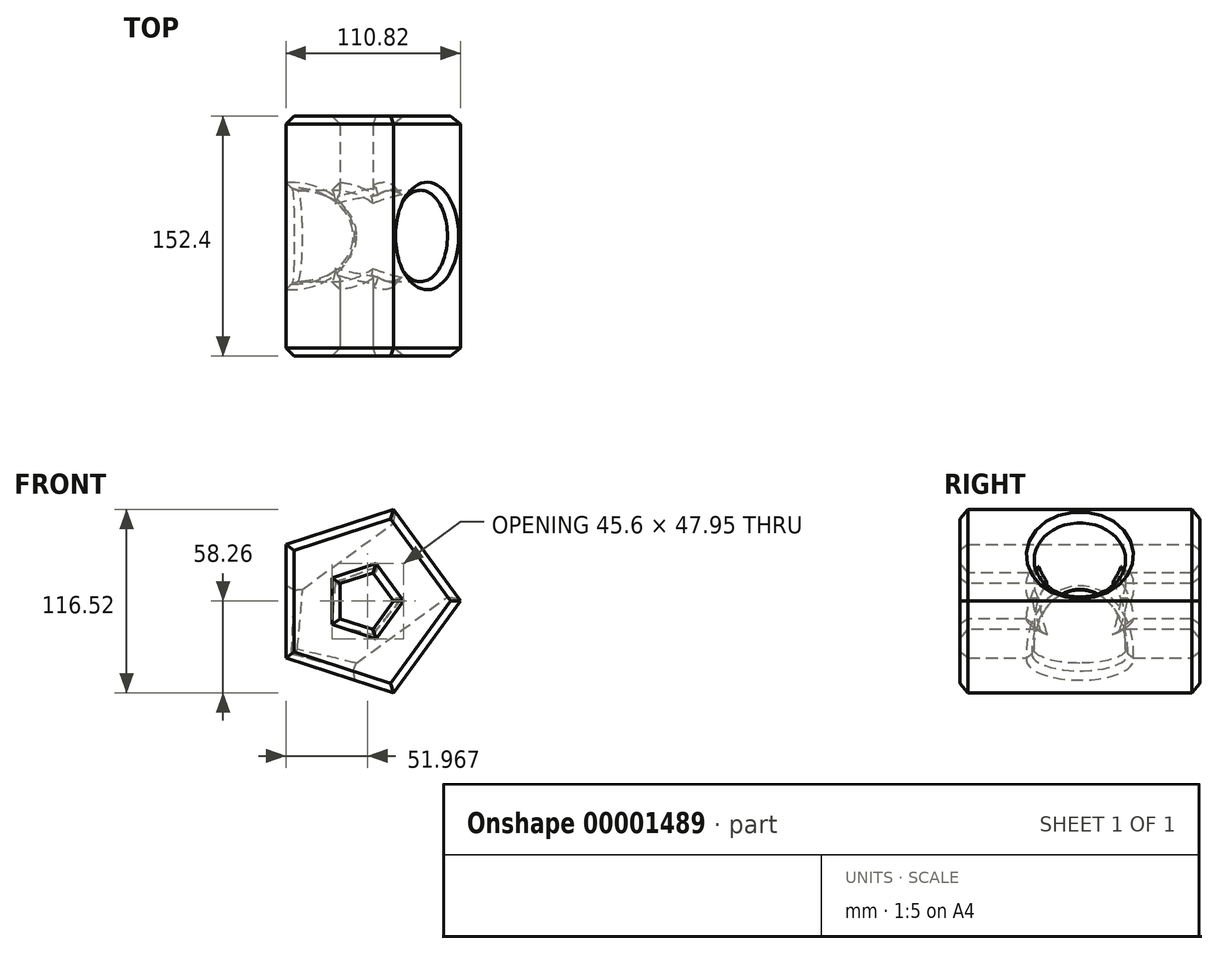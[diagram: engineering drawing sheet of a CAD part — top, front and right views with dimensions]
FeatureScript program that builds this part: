
annotation { "Feature Type Name" : "Feature", "Feature Type Description" : "" }
export const myFeature = defineFeature(function(context is Context, id is Id, definition is map)
    precondition{}
    {
        {
            var Q0;
            Q0=qCreatedBy(makeId("Front.planeOp"),FACE);
            var sketch = newSketch(context, id + "F0", { "sketchPlane" : qUnion([Q0])});
            skCircle(sketch, "E0.cCircle", {"center": v(0, 0) * mm, "radius": 49.56 * mm, "construction": true});
            skLineSegment(sketch, "E0.0", {"start": v(-49.56, -36) * mm, "end": v(-49.56, 36) * mm});
            skLineSegment(sketch, "E0.1", {"start": v(-49.56, 36) * mm, "end": v(18.93, 58.26) * mm});
            skLineSegment(sketch, "E0.2", {"start": v(18.93, 58.26) * mm, "end": v(61.26, 0) * mm});
            skLineSegment(sketch, "E0.3", {"start": v(61.26, 0) * mm, "end": v(18.93, -58.26) * mm});
            skLineSegment(sketch, "E0.4", {"start": v(18.93, -58.26) * mm, "end": v(-49.56, -36) * mm});
            skPoint(sketch, "E0.0.midPoint", {"position": v(-49.56, 0) * mm});
            skLineSegment(sketch, "E1", {"start": v(-49.56, 36) * mm, "end": v(41.4, -27.24) * mm});
            skSolve(sketch);
        }
        {
            var Q0;
            Q0=makeQuery(id+"F0.imprint","IMPRINT",FACE,{"disambiguationData":[TD([[makeQuery(id+"F0.imprint","IMPRINT",EDGE,{"derivedFrom":sQuery(id+"F0.wireOp",EDGE,"E0.0")}),-1.0]])]});
            extrude(context, id + "F1", {"entities" : qUnion([Q0]), "depth" : 152.4 * mm});
        }
        {
            var Q0;
            Q0=makeQuery(id+"F1.opExtrude","SWEPT_FACE",FACE,{"disambiguationData":[OSD([sQuery(id+"F0.wireOp",EDGE,"E0.2")])]});
            var sketch = newSketch(context, id + "F2", { "sketchPlane" : qUnion([Q0])});
            skLineSegment(sketch, "E2", {"start": v(0, 0) * mm, "end": v(-152.4, 0) * mm, "construction": true});
            skLineSegment(sketch, "E3", {"start": v(-76.2, 36) * mm, "end": v(-76.2, -36) * mm, "construction": true});
            skCircle(sketch, "E4", {"center": v(-76.2, 0) * mm, "radius": 29.02 * mm});
            skSolve(sketch);
        }
        {
            var Q0;
            Q0=makeQuery(id+"F2.imprint","IMPRINT",FACE,{"disambiguationData":[TD([[makeQuery(id+"F2.imprint","IMPRINT",EDGE,{"derivedFrom":sQuery(id+"F2.wireOp",EDGE,"E4")}),1.0]])]});
            extrude(context, id + "F3", {"entities" : qUnion([Q0]), "operationType" : NewBodyOperationType.REMOVE, "endBound" : BoundingType.THROUGH_ALL, "oppositeDirection" : true, "depth" : 25.4 * mm});
        }
        {
            var Q0;
            Q0=makeQuery(id+"F1.opExtrude","CAP_FACE",FACE,{"disambiguationData":[OSD([sQuery(id+"F0.wireOp",EDGE,"E0.0"),sQuery(id+"F0.wireOp",EDGE,"E0.1"),sQuery(id+"F0.wireOp",EDGE,"E0.2"),sQuery(id+"F0.wireOp",EDGE,"E0.3"),sQuery(id+"F0.wireOp",EDGE,"E0.4")])],"isStart":false});
            var sketch = newSketch(context, id + "F4", { "sketchPlane" : qUnion([Q0])});
            skLineSegment(sketch, "E5", {"start": v(61.26, 0) * mm, "end": v(-49.56, 0) * mm, "construction": true});
            skLineSegment(sketch, "E6", {"start": v(18.93, 58.26) * mm, "end": v(18.93, -58.26) * mm, "construction": true});
            skCircle(sketch, "E7.cCircle", {"center": v(0, 0) * mm, "radius": 15.31 * mm, "construction": true});
            skLineSegment(sketch, "E7.0", {"start": v(18.93, 0) * mm, "end": v(5.85, -18) * mm});
            skLineSegment(sketch, "E7.1", {"start": v(5.85, -18) * mm, "end": v(-15.31, -11.13) * mm});
            skLineSegment(sketch, "E7.2", {"start": v(-15.31, -11.13) * mm, "end": v(-15.31, 11.13) * mm});
            skLineSegment(sketch, "E7.3", {"start": v(-15.31, 11.13) * mm, "end": v(5.85, 18) * mm});
            skLineSegment(sketch, "E7.4", {"start": v(5.85, 18) * mm, "end": v(18.93, 0) * mm});
            skPoint(sketch, "E7.0.midPoint", {"position": v(12.39, -9) * mm});
            skSolve(sketch);
        }
        {
            var Q0;
            Q0=makeQuery(id+"F4.imprint","IMPRINT",FACE,{"disambiguationData":[TD([[makeQuery(id+"F4.imprint","IMPRINT",EDGE,{"derivedFrom":sQuery(id+"F4.wireOp",EDGE,"E7.0")}),-1.0]])]});
            extrude(context, id + "F5", {"entities" : qUnion([Q0]), "operationType" : NewBodyOperationType.REMOVE, "endBound" : BoundingType.THROUGH_ALL, "oppositeDirection" : true, "depth" : 25.4 * mm});
        }
        {
            var Q0;
            Q0=makeQuery(id+"F1.opExtrude","CAP_FACE",FACE,{"disambiguationData":[OSD([sQuery(id+"F0.wireOp",EDGE,"E0.0"),sQuery(id+"F0.wireOp",EDGE,"E0.1"),sQuery(id+"F0.wireOp",EDGE,"E0.2"),sQuery(id+"F0.wireOp",EDGE,"E0.3"),sQuery(id+"F0.wireOp",EDGE,"E0.4")])],"isStart":false});
            var Q1;
            Q1=makeQuery(id+"F1.opExtrude","CAP_FACE",FACE,{"disambiguationData":[OSD([sQuery(id+"F0.wireOp",EDGE,"E0.0"),sQuery(id+"F0.wireOp",EDGE,"E0.1"),sQuery(id+"F0.wireOp",EDGE,"E0.2"),sQuery(id+"F0.wireOp",EDGE,"E0.3"),sQuery(id+"F0.wireOp",EDGE,"E0.4")])],"isStart":true});
            var Q2;
            Q2=makeQuery(id+"F3.boolean.opBoolean","COPY",EDGE,{"derivedFrom":makeQuery(id+"F3.opExtrude","CAP_EDGE",EDGE,{"disambiguationData":[OSD([sQuery(id+"F2.wireOp",EDGE,"E4")])],"isStart":true})});
            var Q3;
            Q3=makeQuery(id+"F3.boolean.opBoolean","INTERSECT",EDGE,{"derivedFrom":[makeQuery(id+"F1.opExtrude","SWEPT_FACE",FACE,{"disambiguationData":[OSD([sQuery(id+"F0.wireOp",EDGE,"E0.4")])]}),makeQuery(id+"F3.opExtrude","SWEPT_FACE",FACE,{"disambiguationData":[OSD([sQuery(id+"F2.wireOp",EDGE,"E4")])]})]});
            var Q4;
            Q4=makeQuery(id+"F3.boolean.opBoolean","INTERSECT",EDGE,{"derivedFrom":[makeQuery(id+"F1.opExtrude","SWEPT_FACE",FACE,{"disambiguationData":[OSD([sQuery(id+"F0.wireOp",EDGE,"E0.0")])]}),makeQuery(id+"F3.opExtrude","SWEPT_FACE",FACE,{"disambiguationData":[OSD([sQuery(id+"F2.wireOp",EDGE,"E4")])]})]});
            chamfer(context, id + "F6", {"entities" : qUnion([Q0, Q1, Q2, Q3, Q4]), "width" : 5.08 * mm, "tangentPropagation" : true});
        }
        {
            var Q0;
            Q0=makeQuery(id+"F3.boolean.opBoolean","COPY",FACE,{"derivedFrom":makeQuery(id+"F3.opExtrude","SWEPT_FACE",FACE,{"disambiguationData":[OSD([sQuery(id+"F2.wireOp",EDGE,"E4")])]})});
            chamfer(context, id + "F7", {"entities" : qUnion([Q0]), "width" : 5.08 * mm, "tangentPropagation" : true});
        }
    });
